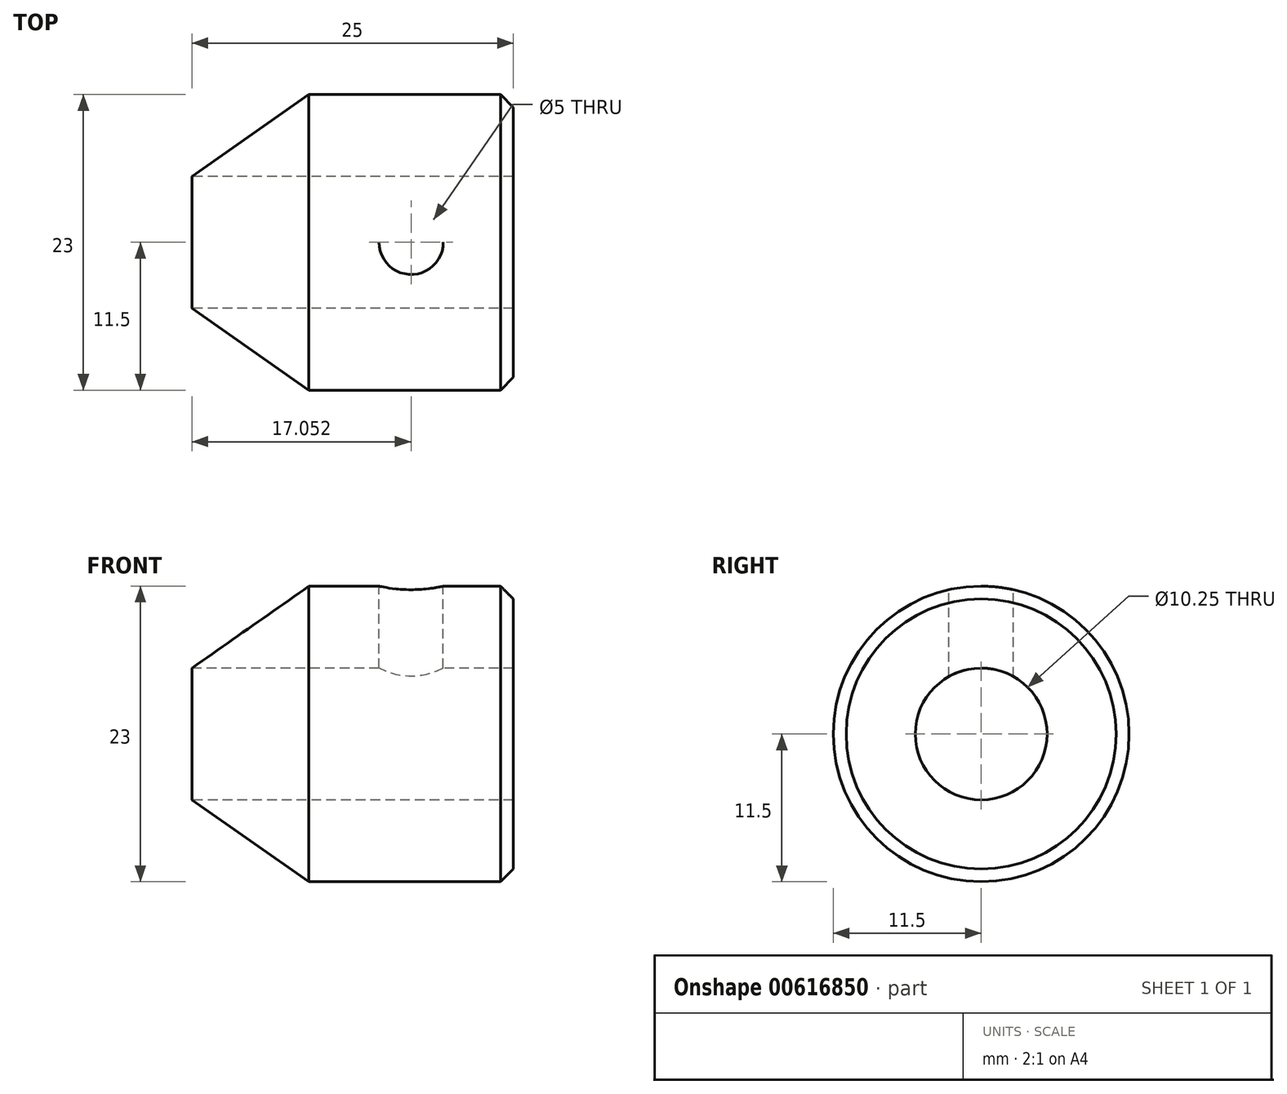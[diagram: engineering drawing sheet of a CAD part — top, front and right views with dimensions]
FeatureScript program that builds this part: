
annotation { "Feature Type Name" : "Feature", "Feature Type Description" : "" }
export const myFeature = defineFeature(function(context is Context, id is Id, definition is map)
    precondition{}
    {
        {
            var Q0;
            Q0=qCreatedBy(makeId("Front.planeOp"),FACE);
            var sketch = newSketch(context, id + "F0", { "sketchPlane" : qUnion([Q0])});
            skLineSegment(sketch, "E0", {"start": v(-25, 5.12) * mm, "end": v(0, 5.12) * mm});
            skLineSegment(sketch, "E1", {"start": v(0, 5.13) * mm, "end": v(0, 11.5) * mm});
            skLineSegment(sketch, "E2", {"start": v(0, 11.5) * mm, "end": v(-15.9, 11.5) * mm});
            skLineSegment(sketch, "E3", {"start": v(-15.9, 11.5) * mm, "end": v(-25, 5.12) * mm});
            skLineSegment(sketch, "E4", {"start": v(-61.4, 0) * mm, "end": v(0, 0) * mm, "construction": true});
            skPoint(sketch, "E5", {"position": v(-7.95, 11.5) * mm});
            skSolve(sketch);
        }
        {
            var Q0;
            Q0 = qSketchRegion(id + "F0", true);
            var Q1;
            Q1=sQuery(id+"F0.wireOp",EDGE,"E4");
            revolve(context, id + "F1", {"surfaceOperationType" : NewSurfaceOperationType.NEW, "entities" : qUnion([Q0]), "axis" : qUnion([Q1]), "revolveType" : RevolveType.FULL});
        }
        {
            var Q0;
            Q0=qCreatedBy(makeId("Top.planeOp"),FACE);
            var sketch = newSketch(context, id + "F2", { "sketchPlane" : qUnion([Q0])});
            skPoint(sketch, "E6.0", {"position": v(-7.95, 0) * mm});
            skSolve(sketch);
        }
        {
            var Q0;
            Q0=sQuery(id+"F2.wireOp",VERTEX,"E6.0");
            var Q1;
            Q1=makeQuery(id+"F1.opRevolve","SWEPT_BODY",BODY,{"disambiguationData":[OSD([sQuery(id+"F0.wireOp",EDGE,"E0"),sQuery(id+"F0.wireOp",EDGE,"E1"),sQuery(id+"F0.wireOp",EDGE,"E2"),sQuery(id+"F0.wireOp",EDGE,"E3")])]});
            hole(context, id + "F3", {"style" : HoleStyle.SIMPLE, "endStyle" : HoleEndStyle.THROUGH, "oppositeDirection" : true, "standardTappedOrClearance" : lookupTablePath({ "standard" : "ISO", "engagement" : "75%", "pitch" : "1 mm", "size" : "M6", "type" : "Tapped" }), "standardBlindInLast" : lookupTablePath({ "standard" : "ISO", "engagement" : "75%", "pitch" : "1 mm", "size" : "M6", "type" : "Tapped" }), "holeDiameter" : 5 * mm, "majorDiameter" : 6 * mm, "showTappedDepth" : true, "isTappedThrough" : true, "tappedDepth" : 12 * mm, "tapClearance" : 3, "locations" : qUnion([Q0]), "scope" : qUnion([Q1]), "startStyle" : HoleStartStyle.PART});
        }
        {
            var Q0;
            Q0=makeQuery(id+"F1.opRevolve","SWEPT_EDGE",EDGE,{"disambiguationData":[OSD([sQuery(id+"F0.wireOp",EDGE,"E1"),sQuery(id+"F0.wireOp",EDGE,"E2")])]});
            chamfer(context, id + "F4", {"entities" : qUnion([Q0]), "width" : 1 * mm, "tangentPropagation" : true});
        }
    });
